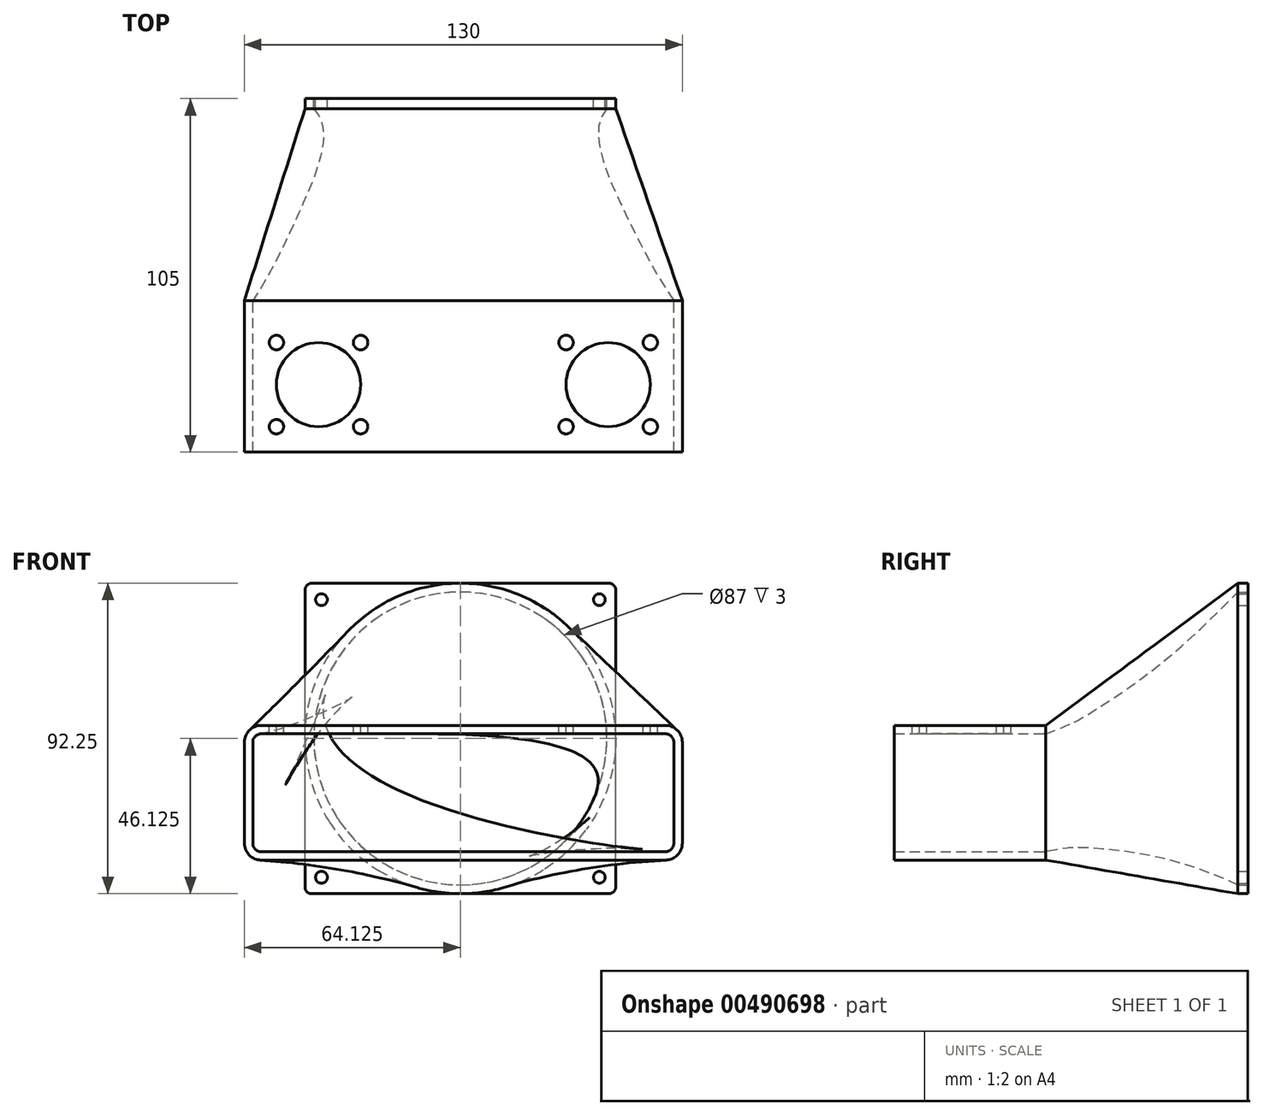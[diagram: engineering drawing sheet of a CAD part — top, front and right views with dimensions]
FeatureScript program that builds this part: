
annotation { "Feature Type Name" : "Feature", "Feature Type Description" : "" }
export const myFeature = defineFeature(function(context is Context, id is Id, definition is map)
    precondition{}
    {
        {
            var Q0;
            Q0=qCreatedBy(makeId("Front.planeOp"),FACE);
            var sketch = newSketch(context, id + "F0", { "sketchPlane" : qUnion([Q0])});
            skLineSegment(sketch, "E0.bottom", {"start": v(0, 0) * mm, "end": v(92.25, 0) * mm});
            skLineSegment(sketch, "E0.top", {"start": v(0, 92.25) * mm, "end": v(92.25, 92.25) * mm});
            skLineSegment(sketch, "E0.left", {"start": v(0, 0) * mm, "end": v(0, 92.25) * mm});
            skLineSegment(sketch, "E0.right", {"start": v(92.25, 0) * mm, "end": v(92.25, 92.25) * mm});
            skCircle(sketch, "E1", {"center": v(46.12, 46.12) * mm, "radius": 43.5 * mm});
            skPoint(sketch, "E1.centerSnap0", {"position": v(0, 46.12) * mm});
            skPoint(sketch, "E1.centerSnap1", {"position": v(46.13, 92.25) * mm});
            skLineSegment(sketch, "E2", {"start": v(0, 46.12) * mm, "end": v(92.25, 46.12) * mm, "construction": true});
            skLineSegment(sketch, "E3", {"start": v(46.12, 92.25) * mm, "end": v(46.13, 0) * mm, "construction": true});
            skCircle(sketch, "E4", {"center": v(4.87, 87.38) * mm, "radius": 1.75 * mm});
            skCircle(sketch, "E5.MirrorC", {"center": v(87.38, 87.38) * mm, "radius": 1.75 * mm});
            skCircle(sketch, "E6.MirrorC", {"center": v(4.88, 4.87) * mm, "radius": 1.75 * mm});
            skCircle(sketch, "E7.MirrorC", {"center": v(87.38, 4.87) * mm, "radius": 1.75 * mm});
            skSolve(sketch);
        }
        {
            var Q0;
            Q0 = qSketchRegion(id + "F0", true);
            extrude(context, id + "F1", {"entities" : qUnion([Q0]), "depth" : 3 * mm, "offsetDistance" : 25 * mm});
        }
        {
            var Q0;
            Q0=makeQuery(id+"F1.opExtrude","SWEPT_EDGE",EDGE,{"disambiguationData":[OSD([sQuery(id+"F0.wireOp",EDGE,"E0.top"),sQuery(id+"F0.wireOp",EDGE,"E0.left")])]});
            var Q1;
            Q1=makeQuery(id+"F1.opExtrude","SWEPT_EDGE",EDGE,{"disambiguationData":[OSD([sQuery(id+"F0.wireOp",EDGE,"E0.top"),sQuery(id+"F0.wireOp",EDGE,"E0.right")])]});
            var Q2;
            Q2=makeQuery(id+"F1.opExtrude","SWEPT_EDGE",EDGE,{"disambiguationData":[OSD([sQuery(id+"F0.wireOp",EDGE,"E0.bottom"),sQuery(id+"F0.wireOp",EDGE,"E0.right")])]});
            var Q3;
            Q3=makeQuery(id+"F1.opExtrude","SWEPT_EDGE",EDGE,{"disambiguationData":[OSD([sQuery(id+"F0.wireOp",EDGE,"E0.bottom"),sQuery(id+"F0.wireOp",EDGE,"E0.left")])]});
            fillet(context, id + "F2", {"entities" : qUnion([Q0, Q1, Q2, Q3]), "radius" : 2 * mm, "tangentPropagation" : true, "allowEdgeOverflow" : false});
        }
        {
            var Q0;
            Q0=qCreatedBy(makeId("Front.planeOp"),FACE);
            cPlane(context, id + "F3", {"entities" : qUnion([Q0]), "cplaneType" : CPlaneType.OFFSET, "offset" : 60 * mm, "width" : 150 * mm, "height" : 150 * mm});
        }
        {
            var Q0;
            Q0=qCreatedBy(id+"F3.planeOp",FACE);
            var sketch = newSketch(context, id + "F4", { "sketchPlane" : qUnion([Q0])});
            skLineSegment(sketch, "E8.bottom", {"start": v(-13, 10) * mm, "end": v(107, 10) * mm});
            skLineSegment(sketch, "E8.top", {"start": v(-13, 50) * mm, "end": v(107, 50) * mm});
            skLineSegment(sketch, "E8.left", {"start": v(-18, 15) * mm, "end": v(-18, 45) * mm});
            skLineSegment(sketch, "E8.right", {"start": v(112, 15) * mm, "end": v(112, 45) * mm});
            skPoint(sketch, "E9.visualSharp", {"position": v(-18, 50) * mm});
            skArc(sketch, "E9.filletArc", {"start": v(-13, 50) * mm, "mid": v(-16.54, 48.54) * mm, "end": v(-18, 45) * mm});
            skPoint(sketch, "E10.visualSharp", {"position": v(-18, 10) * mm});
            skArc(sketch, "E10.filletArc", {"start": v(-18, 15) * mm, "mid": v(-16.54, 11.46) * mm, "end": v(-13, 10) * mm});
            skPoint(sketch, "E11.visualSharp", {"position": v(112, 10) * mm});
            skArc(sketch, "E11.filletArc", {"start": v(107, 10) * mm, "mid": v(110.54, 11.46) * mm, "end": v(112, 15) * mm});
            skPoint(sketch, "E12.visualSharp", {"position": v(112, 50) * mm});
            skArc(sketch, "E12.filletArc", {"start": v(112, 45) * mm, "mid": v(110.54, 48.54) * mm, "end": v(107, 50) * mm});
            skSolve(sketch);
        }
        {
            var Q0;
            Q0=makeQuery(id+"F1.opExtrude","CAP_FACE",FACE,{"disambiguationData":[OSD([sQuery(id+"F0.wireOp",EDGE,"E0.bottom"),sQuery(id+"F0.wireOp",EDGE,"E0.top"),sQuery(id+"F0.wireOp",EDGE,"E0.left"),sQuery(id+"F0.wireOp",EDGE,"E0.right"),sQuery(id+"F0.wireOp",EDGE,"E1"),sQuery(id+"F0.wireOp",EDGE,"E4"),sQuery(id+"F0.wireOp",EDGE,"E5.MirrorC"),sQuery(id+"F0.wireOp",EDGE,"E6.MirrorC"),sQuery(id+"F0.wireOp",EDGE,"E7.MirrorC")])],"isStart":false});
            var sketch = newSketch(context, id + "F5", { "sketchPlane" : qUnion([Q0])});
            skArc(sketch, "E13", {"start": v(10.37, 75.27) * mm, "mid": v(0.08, 48.85) * mm, "end": v(7.19, 21.4) * mm});
            skArc(sketch, "E14", {"start": v(25.34, 87.3) * mm, "mid": v(17.22, 82.07) * mm, "end": v(10.37, 75.27) * mm});
            skArc(sketch, "E15", {"start": v(21.75, 6.97) * mm, "mid": v(46.55, 0) * mm, "end": v(71.2, 7.42) * mm});
            skArc(sketch, "E16", {"start": v(7.19, 21.4) * mm, "mid": v(13.66, 13.36) * mm, "end": v(21.75, 6.97) * mm});
            skArc(sketch, "E17", {"start": v(73.16, 83.5) * mm, "mid": v(49.78, 92.1) * mm, "end": v(25.34, 87.3) * mm});
            skArc(sketch, "E18", {"start": v(84.98, 70.98) * mm, "mid": v(79.66, 77.8) * mm, "end": v(73.16, 83.5) * mm});
            skArc(sketch, "E19", {"start": v(83.5, 19.1) * mm, "mid": v(92.23, 44.81) * mm, "end": v(84.98, 70.98) * mm});
            skArc(sketch, "E20", {"start": v(71.2, 7.42) * mm, "mid": v(77.9, 12.69) * mm, "end": v(83.5, 19.1) * mm});
            skSolve(sketch);
        }
        {
            var Q1;
            Q1 = qSketchRegion(id + "F4", true);
            var Q2;
            Q2 = qSketchRegion(id + "F5", true);
            var Q3;
            Q3=sQuery(id+"F5.wireOp",VERTEX,"E15.end");
            var Q4;
            Q4=sQuery(id+"F4.wireOp",VERTEX,"E11.filletArc.start");
            loft(context, id + "F6", {"operationType" : NewBodyOperationType.ADD, "sheetProfilesArray" : [{ "sheetProfileEntities" : qUnion([Q1]) }, { "sheetProfileEntities" : qUnion([Q2]) }], "guidesArray" : [{ "guideEntities" : qUnion([]), "guideDerivativeType" : LoftGuideDerivativeType.MATCH_TANGENT, "guideDerivativeMagnitude" : 1 }], "matchConnections" : true, "connections" : [{ "connectionEntities" : qUnion([Q3, Q4]), "connectionEdgeQueries" : qUnion([]), "connectionEdgeParameters" : [] }]});
        }
        {
            var Q0;
            {var subQ0=sQuery(id+"F0.wireOp",EDGE,"E0.left");var subQ1=sQuery(id+"F0.wireOp",EDGE,"E0.top");var subQ2=sQuery(id+"F0.wireOp",EDGE,"E4");var subQ3=makeQuery(id+"F1.opExtrude","CAP_FACE",FACE,{"disambiguationData":[OSD([sQuery(id+"F0.wireOp",EDGE,"E0.bottom"),subQ1,subQ0,sQuery(id+"F0.wireOp",EDGE,"E0.right"),sQuery(id+"F0.wireOp",EDGE,"E1"),subQ2,sQuery(id+"F0.wireOp",EDGE,"E5.MirrorC"),sQuery(id+"F0.wireOp",EDGE,"E6.MirrorC"),sQuery(id+"F0.wireOp",EDGE,"E7.MirrorC")])],"isStart":false});Q0=makeQuery(id+"F6.boolean.opBoolean","SPLIT",FACE,{"disambiguationData":[TD([makeQuery(id+"F1.opExtrude","SWEPT_FACE",FACE,{"disambiguationData":[OSD([subQ2])]})])],"derivedFrom":subQ3});}
            var sketch = newSketch(context, id + "F7", { "sketchPlane" : qUnion([Q0])});
            skArc(sketch, "E21", {"start": v(11.58, 72.57) * mm, "mid": v(2.65, 47.64) * mm, "end": v(9.83, 22.15) * mm});
            skArc(sketch, "E22", {"start": v(22, 82.33) * mm, "mid": v(16.4, 77.88) * mm, "end": v(11.58, 72.57) * mm});
            skArc(sketch, "E23", {"start": v(82.55, 69.9) * mm, "mid": v(77.11, 76.65) * mm, "end": v(70.45, 82.2) * mm});
            skArc(sketch, "E24", {"start": v(70.45, 82.2) * mm, "mid": v(46.25, 89.62) * mm, "end": v(22, 82.33) * mm});
            skArc(sketch, "E25", {"start": v(70.38, 10.02) * mm, "mid": v(75.97, 14.48) * mm, "end": v(80.75, 19.8) * mm});
            skArc(sketch, "E26", {"start": v(80.75, 19.8) * mm, "mid": v(89.6, 44.56) * mm, "end": v(82.55, 69.9) * mm});
            skArc(sketch, "E27", {"start": v(23.08, 9.23) * mm, "mid": v(46.84, 2.63) * mm, "end": v(70.38, 10.02) * mm});
            skArc(sketch, "E28", {"start": v(9.83, 22.15) * mm, "mid": v(15.76, 14.98) * mm, "end": v(23.08, 9.23) * mm});
            skSolve(sketch);
        }
        {
            var Q0;
            Q0=qCreatedBy(id+"F3.planeOp",FACE);
            var sketch = newSketch(context, id + "F8", { "sketchPlane" : qUnion([Q0])});
            skArc(sketch, "E29.0", {"start": v(112, 45) * mm, "mid": v(110.54, 48.54) * mm, "end": v(107, 50) * mm, "construction": true});
            skArc(sketch, "E29.1", {"start": v(-18, 15) * mm, "mid": v(-16.54, 11.46) * mm, "end": v(-13, 10) * mm, "construction": true});
            skLineSegment(sketch, "E29.2", {"start": v(-18, 15) * mm, "end": v(-18, 45) * mm, "construction": true});
            skArc(sketch, "E29.3", {"start": v(-13, 50) * mm, "mid": v(-16.54, 48.54) * mm, "end": v(-18, 45) * mm, "construction": true});
            skLineSegment(sketch, "E29.4", {"start": v(-13, 10) * mm, "end": v(107, 10) * mm, "construction": true});
            skLineSegment(sketch, "E29.5", {"start": v(-13, 50) * mm, "end": v(107, 50) * mm, "construction": true});
            skArc(sketch, "E29.6", {"start": v(107, 10) * mm, "mid": v(110.54, 11.46) * mm, "end": v(112, 15) * mm, "construction": true});
            skLineSegment(sketch, "E29.7", {"start": v(112, 15) * mm, "end": v(112, 45) * mm, "construction": true});
            skLineSegment(sketch, "E30.0", {"start": v(-13, 12.5) * mm, "end": v(107, 12.5) * mm});
            skArc(sketch, "E30.1", {"start": v(-15.5, 15) * mm, "mid": v(-14.77, 13.23) * mm, "end": v(-13, 12.5) * mm});
            skArc(sketch, "E30.2", {"start": v(107, 12.5) * mm, "mid": v(108.77, 13.23) * mm, "end": v(109.5, 15) * mm});
            skLineSegment(sketch, "E30.3", {"start": v(-15.5, 15) * mm, "end": v(-15.5, 45) * mm});
            skLineSegment(sketch, "E30.4", {"start": v(109.5, 15) * mm, "end": v(109.5, 45) * mm});
            skArc(sketch, "E30.5", {"start": v(109.5, 45) * mm, "mid": v(108.77, 46.77) * mm, "end": v(107, 47.5) * mm});
            skLineSegment(sketch, "E30.6", {"start": v(-13, 47.5) * mm, "end": v(107, 47.5) * mm});
            skArc(sketch, "E30.7", {"start": v(-13, 47.5) * mm, "mid": v(-14.77, 46.77) * mm, "end": v(-15.5, 45) * mm});
            skSolve(sketch);
        }
        {
            var Q1;
            Q1 = qSketchRegion(id + "F7", true);
            var Q2;
            Q2 = qSketchRegion(id + "F8", true);
            var Q3;
            Q3=sQuery(id+"F8.wireOp",VERTEX,"E30.7.start");
            var Q4;
            Q4=sQuery(id+"F7.wireOp",VERTEX,"E23.start");
            loft(context, id + "F9", {"operationType" : NewBodyOperationType.REMOVE, "sheetProfilesArray" : [{ "sheetProfileEntities" : qUnion([Q1]) }, { "sheetProfileEntities" : qUnion([Q2]) }], "matchConnections" : true, "connections" : [{ "connectionEntities" : qUnion([Q3, Q4]), "connectionEdgeQueries" : qUnion([]), "connectionEdgeParameters" : [] }]});
        }
        {
            var Q0;
            Q0=qCreatedBy(id+"F3.planeOp",FACE);
            var sketch = newSketch(context, id + "F10", { "sketchPlane" : qUnion([Q0])});
            skLineSegment(sketch, "E31.0", {"start": v(-13, 10) * mm, "end": v(107, 10) * mm});
            skLineSegment(sketch, "E31.1", {"start": v(-13, 12.5) * mm, "end": v(107, 12.5) * mm});
            skArc(sketch, "E31.2", {"start": v(-18, 15) * mm, "mid": v(-16.54, 11.46) * mm, "end": v(-13, 10) * mm});
            skArc(sketch, "E31.3", {"start": v(-15.5, 15) * mm, "mid": v(-14.77, 13.23) * mm, "end": v(-13, 12.5) * mm});
            skLineSegment(sketch, "E31.4", {"start": v(-18, 15) * mm, "end": v(-18, 45) * mm});
            skLineSegment(sketch, "E31.5", {"start": v(-15.5, 15) * mm, "end": v(-15.5, 45) * mm});
            skArc(sketch, "E31.6", {"start": v(-13, 47.5) * mm, "mid": v(-14.77, 46.77) * mm, "end": v(-15.5, 45) * mm});
            skArc(sketch, "E31.7", {"start": v(-13, 50) * mm, "mid": v(-16.54, 48.54) * mm, "end": v(-18, 45) * mm});
            skLineSegment(sketch, "E31.8", {"start": v(-13, 50) * mm, "end": v(107, 50) * mm});
            skLineSegment(sketch, "E31.9", {"start": v(-13, 47.5) * mm, "end": v(107, 47.5) * mm});
            skArc(sketch, "E31.10", {"start": v(112, 45) * mm, "mid": v(110.54, 48.54) * mm, "end": v(107, 50) * mm});
            skArc(sketch, "E31.11", {"start": v(109.5, 45) * mm, "mid": v(108.77, 46.77) * mm, "end": v(107, 47.5) * mm});
            skLineSegment(sketch, "E31.12", {"start": v(112, 15) * mm, "end": v(112, 45) * mm});
            skLineSegment(sketch, "E31.13", {"start": v(109.5, 15) * mm, "end": v(109.5, 45) * mm});
            skArc(sketch, "E31.14", {"start": v(107, 10) * mm, "mid": v(110.54, 11.46) * mm, "end": v(112, 15) * mm});
            skArc(sketch, "E31.15", {"start": v(107, 12.5) * mm, "mid": v(108.77, 13.23) * mm, "end": v(109.5, 15) * mm});
            skSolve(sketch);
        }
        {
            var Q0;
            Q0 = qSketchRegion(id + "F10", true);
            extrude(context, id + "F11", {"entities" : qUnion([Q0]), "operationType" : NewBodyOperationType.ADD, "depth" : 45 * mm, "offsetDistance" : 25 * mm});
        }
        {
            var Q0;
            Q0=makeQuery(id+"F11.opExtrude","SWEPT_FACE",FACE,{"disambiguationData":[OSD([sQuery(id+"F10.wireOp",EDGE,"E31.8")])]});
            var sketch = newSketch(context, id + "F12", { "sketchPlane" : qUnion([Q0])});
            skLineSegment(sketch, "E32", {"start": v(47, -105) * mm, "end": v(47, -60) * mm, "construction": true});
            skCircle(sketch, "E33", {"center": v(4, -85) * mm, "radius": 12.5 * mm});
            skCircle(sketch, "E34", {"center": v(-8.5, -72.5) * mm, "radius": 2.15 * mm});
            skCircle(sketch, "E35", {"center": v(16.5, -72.5) * mm, "radius": 2.15 * mm});
            skCircle(sketch, "E36", {"center": v(16.5, -97.5) * mm, "radius": 2.15 * mm});
            skCircle(sketch, "E37", {"center": v(-8.5, -97.5) * mm, "radius": 2.15 * mm});
            skCircle(sketch, "E38.MirrorC", {"center": v(102.5, -72.5) * mm, "radius": 2.15 * mm});
            skCircle(sketch, "E39.MirrorC", {"center": v(77.5, -72.5) * mm, "radius": 2.15 * mm});
            skCircle(sketch, "E40.MirrorC", {"center": v(90, -85) * mm, "radius": 12.5 * mm});
            skCircle(sketch, "E41.MirrorC", {"center": v(77.5, -97.5) * mm, "radius": 2.15 * mm});
            skCircle(sketch, "E42.MirrorC", {"center": v(102.5, -97.5) * mm, "radius": 2.15 * mm});
            skSolve(sketch);
        }
        {
            var Q0;
            Q0 = qSketchRegion(id + "F12", true);
            var Q1;
            Q1=makeQuery(id+"F11.opExtrude","SWEPT_FACE",FACE,{"disambiguationData":[OSD([sQuery(id+"F10.wireOp",EDGE,"E31.1")])]});
            extrude(context, id + "F13", {"entities" : qUnion([Q0]), "operationType" : NewBodyOperationType.REMOVE, "endBound" : BoundingType.UP_TO_SURFACE, "oppositeDirection" : true, "depth" : 25 * mm, "endBoundEntityFace" : qUnion([Q1]), "offsetDistance" : 25 * mm});
        }
    });
